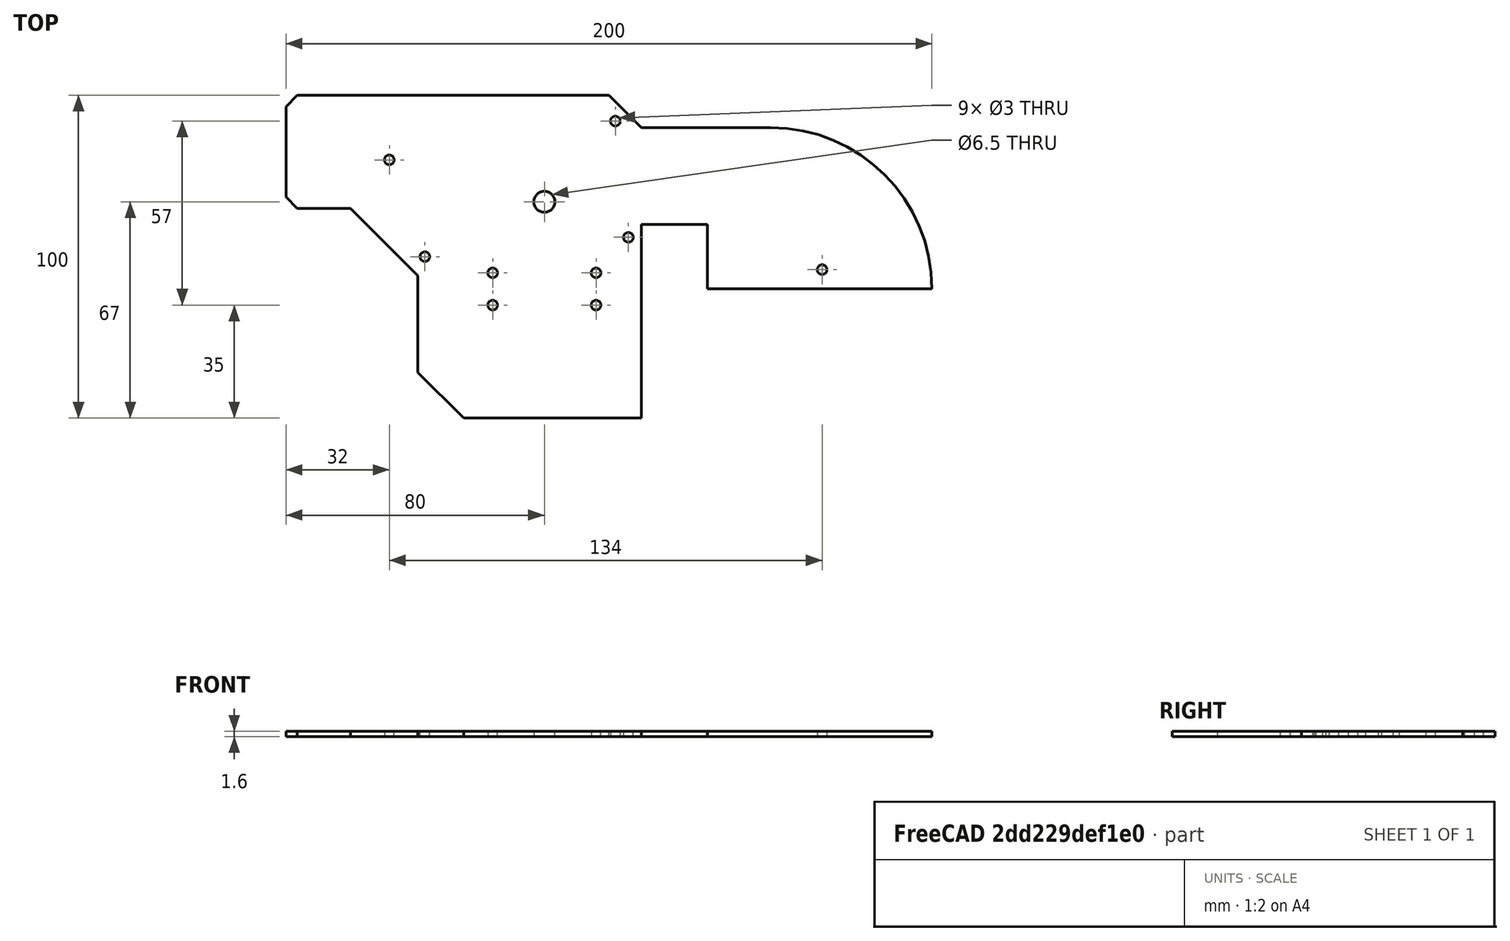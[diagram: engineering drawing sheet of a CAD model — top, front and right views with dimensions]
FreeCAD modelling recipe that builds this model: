
FCSTD DOCUMENT  (FreeCAD 0.18.4R)
Label: feeder-pcb
License: All rights reserved
LicenseURL: http://en.wikipedia.org/wiki/All_rights_reserved
objects: Sketcher::SketchObject×1, PartDesign::Pad×1, PartDesign::Body×1
note: 4 computed .brp shape members not serialized (recipe doc carries the construction recipe); baked Part::Feature solids carry a one-line shape summary decoded from their .brp

FEATURE [Sketcher::SketchObject] Sketch
  MapMode = 5
  Support = -> [XY_Plane]
  sketch-geometry (51):
    g0: LineSegment StartX=20.5 StartY=0 StartZ=0 EndX=20.5 EndY=20 EndZ=0
    g1: LineSegment StartX=20.5 StartY=20 StartZ=0 EndX=0 EndY=20 EndZ=0
    g2: LineSegment StartX=0 StartY=20 StartZ=0 EndX=0 EndY=-40 EndZ=0
    g3: LineSegment StartX=0 StartY=-40 StartZ=0 EndX=-55 EndY=-40 EndZ=0
    g4: LineSegment StartX=-55 StartY=-40 StartZ=0 EndX=-69.1421 EndY=-25.8579 EndZ=0
    g5: LineSegment StartX=-69.1421 StartY=4.14214 StartZ=0 EndX=-90 EndY=25 EndZ=0
    g6: LineSegment StartX=-110 StartY=28.5355 StartZ=0 EndX=-110 EndY=56.4645 EndZ=0
    g7: LineSegment StartX=-110 StartY=56.4645 StartZ=0 EndX=-106.464 EndY=60 EndZ=0
    g8: LineSegment StartX=-106.464 StartY=60 StartZ=0 EndX=-10 EndY=60 EndZ=0
    g9: LineSegment StartX=-10 StartY=60 StartZ=0 EndX=0 EndY=50 EndZ=0
    g10: LineSegment StartX=0 StartY=50 StartZ=0 EndX=40 EndY=50 EndZ=0
    g11: ArcOfCircle CenterX=40 CenterY=0 CenterZ=0 NormalX=0 NormalY=0 NormalZ=1 AngleXU=0 Radius=50 StartAngle=0 EndAngle=1.5708
    g12: LineSegment StartX=20.5 StartY=0 StartZ=0 EndX=90 EndY=0 EndZ=0
    g13: ArcOfCircle [constr] CenterX=40 CenterY=0 CenterZ=0 NormalX=0 NormalY=0 NormalZ=1 AngleXU=0 Radius=46.5 StartAngle=0 EndAngle=1.5708
    g14: LineSegment [constr] StartX=40 StartY=46.5 StartZ=0 EndX=-45 EndY=46.5 EndZ=0
    g15: ArcOfCircle [constr] CenterX=-45 CenterY=-1.9e-15 CenterZ=0 NormalX=0 NormalY=0 NormalZ=1 AngleXU=0 Radius=46.5 StartAngle=1.5708 EndAngle=2.35619
    g16: LineSegment [constr] StartX=-87.8805 StartY=22.8805 StartZ=0 EndX=-77.8805 EndY=32.8805 EndZ=0
    g17: ArcOfCircle [constr] CenterX=40 CenterY=0 CenterZ=0 NormalX=0 NormalY=0 NormalZ=1 AngleXU=0 Radius=48 StartAngle=0 EndAngle=1.5708
    g18: LineSegment [constr] StartX=40 StartY=48 StartZ=0 EndX=-45 EndY=48 EndZ=0
    g19: ArcOfCircle [constr] CenterX=-45 CenterY=-1.9e-15 CenterZ=0 NormalX=0 NormalY=0 NormalZ=1 AngleXU=0 Radius=48 StartAngle=1.5708 EndAngle=2.35619
    g20: LineSegment [constr] StartX=-78.9411 StartY=33.9412 StartZ=0 EndX=-88.9411 EndY=23.9411 EndZ=0
    g21: ArcOfCircle [constr] CenterX=40 CenterY=0 CenterZ=0 NormalX=0 NormalY=0 NormalZ=1 AngleXU=0 Radius=20 StartAngle=0 EndAngle=1.5708
    g22: LineSegment [constr] StartX=40 StartY=20 StartZ=0 EndX=20.5 EndY=20 EndZ=0
    g23: LineSegment [constr] StartX=0 StartY=20 StartZ=0 EndX=-45 EndY=20 EndZ=0
    g24: LineSegment [constr] StartX=-69.1421 StartY=4.14214 StartZ=0 EndX=-59.1421 EndY=14.1421 EndZ=0
    g25: ArcOfCircle [constr] CenterX=-45 CenterY=-1.9e-15 CenterZ=0 NormalX=0 NormalY=0 NormalZ=1 AngleXU=0 Radius=20 StartAngle=1.5708 EndAngle=2.35619
    g26: LineSegment StartX=-69.1421 StartY=-25.8579 StartZ=0 EndX=-69.1421 EndY=4.14214 EndZ=0
    g27: LineSegment [constr] StartX=-102 StartY=55 StartZ=0 EndX=-90 EndY=55 EndZ=0
    g28: LineSegment [constr] StartX=-90 StartY=55 StartZ=0 EndX=-90 EndY=30 EndZ=0
    g29: LineSegment [constr] StartX=-90 StartY=30 StartZ=0 EndX=-102 EndY=30 EndZ=0
    g30: LineSegment [constr] StartX=-102 StartY=30 StartZ=0 EndX=-102 EndY=55 EndZ=0
    g31: LineSegment [constr] StartX=0 StartY=75 StartZ=0 EndX=-75 EndY=75 EndZ=0
    g32: LineSegment StartX=-90 StartY=25 StartZ=0 EndX=-106.464 EndY=25 EndZ=0
    g33: LineSegment [constr] StartX=-90 StartY=55 StartZ=0 EndX=-90 EndY=80 EndZ=0
    g34: LineSegment StartX=-106.464 StartY=25 StartZ=0 EndX=-110 EndY=28.5355 EndZ=0
    g35: LineSegment [constr] StartX=40 StartY=20 StartZ=0 EndX=40 EndY=0 EndZ=0
    g36: Circle CenterX=56 CenterY=6 CenterZ=0 NormalX=0 NormalY=0 NormalZ=1 AngleXU=0 Radius=1.5
    g37: Circle CenterX=-8 CenterY=52 CenterZ=0 NormalX=0 NormalY=0 NormalZ=1 AngleXU=0 Radius=1.5
    g38: Circle CenterX=-78 CenterY=40 CenterZ=0 NormalX=0 NormalY=0 NormalZ=1 AngleXU=0 Radius=1.5
    g39: Circle CenterX=-4 CenterY=16 CenterZ=0 NormalX=0 NormalY=0 NormalZ=1 AngleXU=0 Radius=1.5
    g40: Circle CenterX=-67 CenterY=10 CenterZ=0 NormalX=0 NormalY=0 NormalZ=1 AngleXU=0 Radius=1.5
    g41: Circle CenterX=-30 CenterY=27 CenterZ=0 NormalX=0 NormalY=0 NormalZ=1 AngleXU=0 Radius=3.25
    g42: LineSegment [constr] StartX=-46 StartY=5 StartZ=0 EndX=-14 EndY=5 EndZ=0
    g43: LineSegment [constr] StartX=-14 StartY=5 StartZ=0 EndX=-14 EndY=-5 EndZ=0
    g44: LineSegment [constr] StartX=-14 StartY=-5 StartZ=0 EndX=-46 EndY=-5 EndZ=0
    g45: LineSegment [constr] StartX=-46 StartY=-5 StartZ=0 EndX=-46 EndY=5 EndZ=0
    g46: LineSegment [constr] StartX=-30 StartY=5 StartZ=0 EndX=-30 EndY=-5 EndZ=0
    g47: Circle CenterX=-46 CenterY=5 CenterZ=0 NormalX=0 NormalY=0 NormalZ=1 AngleXU=0 Radius=1.5
    g48: Circle CenterX=-14 CenterY=5 CenterZ=0 NormalX=0 NormalY=0 NormalZ=1 AngleXU=0 Radius=1.5
    g49: Circle CenterX=-14 CenterY=-5 CenterZ=0 NormalX=0 NormalY=0 NormalZ=1 AngleXU=0 Radius=1.5
    g50: Circle CenterX=-46 CenterY=-5 CenterZ=0 NormalX=0 NormalY=0 NormalZ=1 AngleXU=0 Radius=1.5
  constraints (152):
    c: PointOnObject(g0,g-1)
    c: Vertical(g0)
    c: Coincident(g0,g1)
    c: PointOnObject(g1,g-2)
    c: Horizontal(g1)
    c: Coincident(g1,g2)
    c: PointOnObject(g2,g-2)
    c: Coincident(g2,g3)
    c: Horizontal(g3)
    c: Coincident(g3,g4)
    c: Vertical(g6)
    c: Coincident(g6,g7)
    c: Horizontal(g8)
    c: Coincident(g8,g9)
    c: Coincident(g9,g10)
    c: Horizontal(g10)
    c: PointOnObject(g11,g-1)
    c: Coincident(g12,g0)
    c: Coincident(g12,g11)
    c: Coincident(g10,g11)
    c: DistanceX(g1,g1) = 20.5
    c: DistanceY(g0,g0) = 20
    c: Diameter(g11) = 100
    c: PointOnObject(g11,g-1)
    c: DistanceX(g-1,g11) = 40
    c: DistanceY(g2,g-1) = 40
    c: Angle(g5,g-1) = 0.785398
    c: Angle(g10,g9) = 2.35619
    c: Distance(g4) = 20
    c: Coincident(g13,g11)
    c: PointOnObject(g13,g12)
    c: Coincident(g14,g13)
    c: Horizontal(g14)
    c: Coincident(g15,g14)
    c: PointOnObject(g16,g5)
    c: Coincident(g16,g15)
    c: Diameter(g13) = 93
    c: Tangent(g15,g14)
    c: Tangent(g15,g16)
    c: Perpendicular(g5,g16)
    c: Coincident(g17,g11)
    c: PointOnObject(g17,g12)
    c: Coincident(g18,g17)
    c: Horizontal(g18)
    c: Diameter(g17) = 96
    c: Tangent(g18,g17)
    c: Coincident(g19,g15)
    c: Coincident(g19,g18)
    c: Coincident(g20,g19)
    c: PointOnObject(g20,g5)
    c: Tangent(g19,g18)
    c: Parallel(g20,g16)
    c: Coincident(g21,g11)
    c: PointOnObject(g21,g12)
    c: Diameter(g21) = 40
    c: Coincident(g22,g21)
    c: Coincident(g22,g0)
    c: Coincident(g23,g1)
    c: Horizontal(g23)
    c: PointOnObject(g24,g5)
    c: Coincident(g25,g15)
    c: Coincident(g25,g23)
    c: Coincident(g24,g25)
    c: Tangent(g23,g25)
    c: Parallel(g16,g24)
    c: Coincident(g26,g4)
    c: Coincident(g26,g5)
    c: Vertical(g26)
    c: Angle(g3,g4) = 2.35619
    c: DistanceX(g3,g-1) = 55
    c: Tangent(g20,g19)
    c: Tangent(g10,g11)
    c: Coincident(g27,g28)
    c: Coincident(g28,g29)
    c: Coincident(g29,g30)
    c: Coincident(g30,g27)
    c: Horizontal(g27)
    c: Horizontal(g29)
    c: Vertical(g28)
    c: Vertical(g30)
    c: DistanceY(g28,g28) = 25
    c: DistanceX(g27,g27) = 12
    c: DistanceX(g15,g-1) = 45
    c: Diameter(g25) = 40
    c: PointOnObject(g31,g-2)
    c: Horizontal(g31)
    c: DistanceY(g1,g31) = 55
    c: DistanceX(g31,g31) = 75
    c: Horizontal(g32)
    c: Coincident(g5,g32)
    c: Coincident(g33,g27)
    c: Vertical(g33)
    c: DistanceY(g33,g33) = 25
    c: PointOnObject(g9,g-2)
    c: Coincident(g6,g34)
    c: Coincident(g32,g34)
    c: Angle(g32,g34) = 2.35619
    c: Distance(g34) = 5
    c: DistanceX(g28,g1) = 90
    c: DistanceY(g-1,g28) = 30
    c: DistanceY(g-1,g8) = 60
    c: Coincident(g7,g8)
    c: Coincident(g35,g21)
    c: Vertical(g35)
    c: Coincident(g11,g35)
    c: Diameter(g36) = 3
    c: Tangent(g24,g25)
    c: DistanceY(g-1,g36) = 6
    c: DistanceX(g-1,g36) = 56
    c: Diameter(g37) = 3
    c: DistanceX(g37,g-1) = 8
    c: DistanceY(g-1,g37) = 52
    c: Diameter(g38) = 3
    c: Diameter(g39) = 3
    c: Diameter(g40) = 3
    c: DistanceX(g39,g-1) = 4
    c: DistanceY(g-1,g39) = 16
    c: DistanceY(g-1,g40) = 10
    c: DistanceX(g40,g-1) = 67
    c: DistanceX(g38,g-1) = 78
    c: DistanceY(g-1,g38) = 40
    c: Angle(g6,g7) = 2.35619
    c: DistanceY(g-1,g32) = 25
    c: Distance(g7) = 5
    c: DistanceX(g6,g-1) = 110
    c: Tangent(g13,g14)
    c: Diameter(g41) = 6.5
    c: DistanceX(g41,g-1) = 30
    c: DistanceY(g-1,g41) = 27
    c: Coincident(g42,g43)
    c: Coincident(g43,g44)
    c: Coincident(g44,g45)
    c: Coincident(g45,g42)
    c: Horizontal(g44)
    c: Vertical(g43)
    c: Vertical(g45)
    c: PointOnObject(g46,g42)
    c: PointOnObject(g46,g44)
    c: Symmetric(g46,g46,g-1)
    c: Symmetric(g42,g42,g46)
    c: DistanceX(g46,g-1) = 30
    c: DistanceY(g43,g43) = 10
    c: DistanceX(g42,g42) = 32
    c: Coincident(g47,g42)
    c: Coincident(g48,g42)
    c: Coincident(g49,g43)
    c: Coincident(g50,g44)
    c: Diameter(g47) = 3
    c: Diameter(g50) = 3
    c: Diameter(g49) = 3
    c: Diameter(g48) = 3
    c: DistanceX(g5,g-1) = 90
FEATURE [PartDesign::Pad] Pad
  Length = 1.6
  Length2 = 100
  Profile = -> Sketch
  Type = 0
FEATURE [PartDesign::Body] Body
  Group = -> [Sketch,Pad]
  Origin = -> Origin
  Tip = -> Pad
